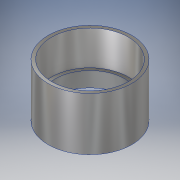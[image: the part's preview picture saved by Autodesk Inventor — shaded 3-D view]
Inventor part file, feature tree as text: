
AUTODESK INVENTOR PART (.ipt)
format: ipt  version: 2017 (Build 210142000, 142)  size: 139,264 bytes
history: native  units: in
note: dims shown in document units (in); Inventor stores cm internally (conversion verified against a paired STEP export)
features: revolve x1, sketch x1
ambient origin geometry x8: Origin, YZ Plane, XZ Plane, XY Plane, X Axis, Y Axis, Z Axis, Center Point
bodies: Solid1 (feature_tree)
feature tree (2):
  revolve  "Revolution1"  [1 undecoded]
  sketch  "Sketch1"  dims[d0=0.25in d1=0.125in d2=105.0deg d3=2.65in d4=0.25in d5=90.0deg d6=4.0in]
note: 1 required parameter value undecoded (feature->parameter linkage not recoverable at this tier; creation-order binding heuristic only, values carry confidence <= 0.55)
